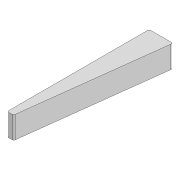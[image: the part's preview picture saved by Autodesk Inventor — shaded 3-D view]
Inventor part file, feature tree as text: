
AUTODESK INVENTOR PART (.ipt)
format: ipt  version: 2020 (Build 240168000, 168)  size: 86,528 bytes
history: native  units: mm
features: extrude x1, sketch x1
ambient origin geometry x8: Origin, YZ Plane, XZ Plane, XY Plane, X Axis, Y Axis, Z Axis, Center Point
bodies: Solid1 (feature_tree)
feature tree (2):
  extrude  "Extrusion1"  Depth=7.0mm
  sketch  "Sketch1"  dims[d0=45.0mm d1=1.22173mm d2=2.0mm d3=0.5mm d4=0.5mm d5=0.5mm d6=7.0mm d7=0.0mm]
